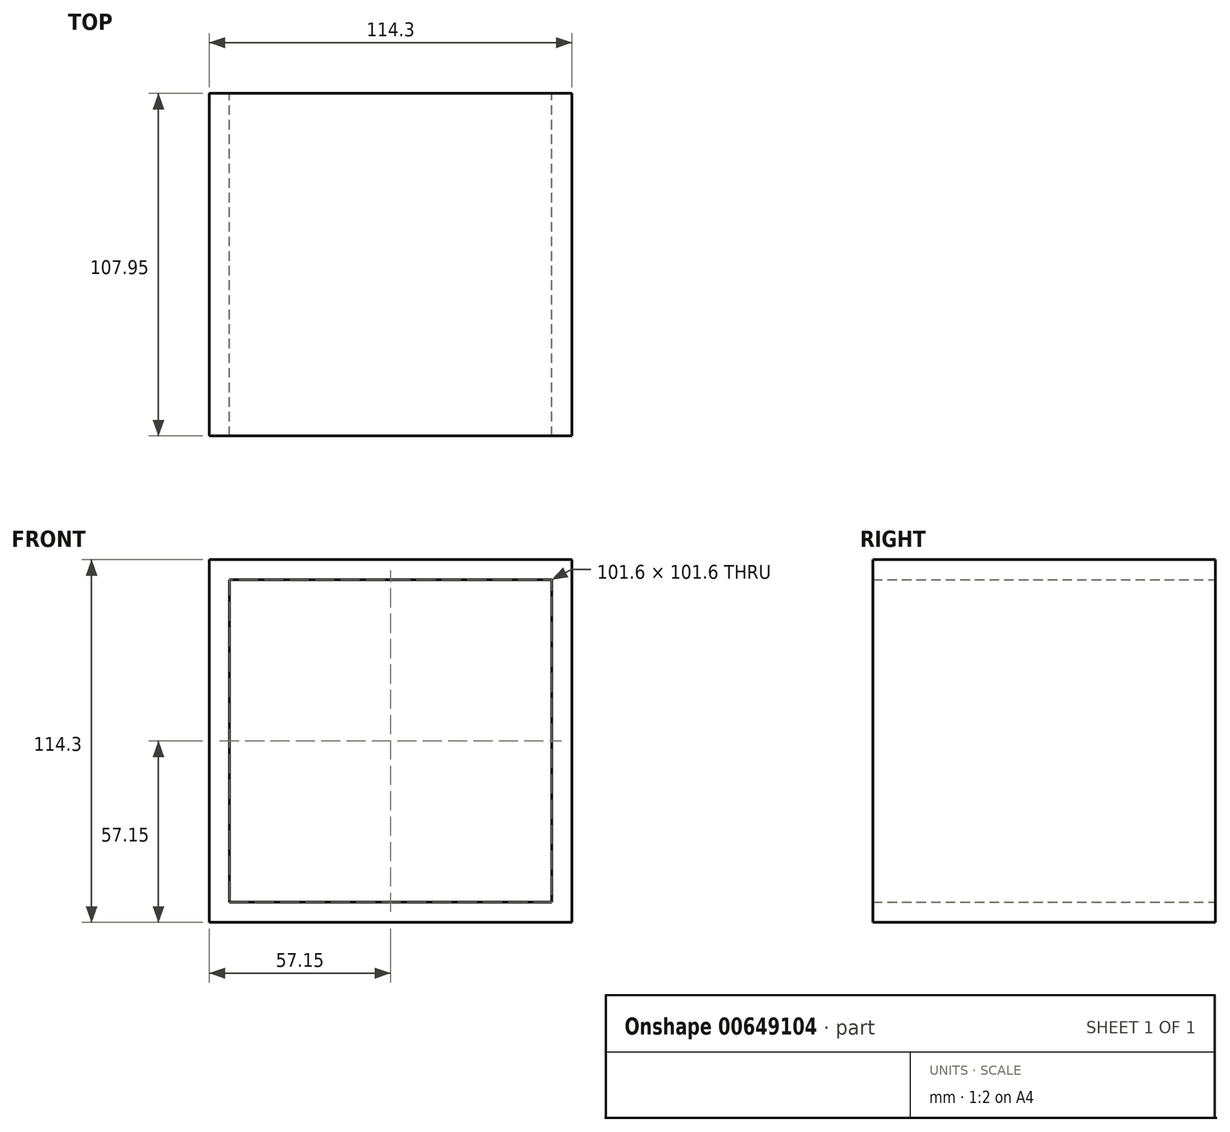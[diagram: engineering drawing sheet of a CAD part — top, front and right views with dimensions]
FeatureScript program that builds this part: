
annotation { "Feature Type Name" : "Feature", "Feature Type Description" : "" }
export const myFeature = defineFeature(function(context is Context, id is Id, definition is map)
    precondition{}
    {
        {
            var Q0;
            Q0=qCreatedBy(makeId("Front.planeOp"),FACE);
            var sketch = newSketch(context, id + "F0", { "sketchPlane" : qUnion([Q0])});
            skLineSegment(sketch, "E0.bottom", {"start": v(50.8, -50.8) * mm, "end": v(-50.8, -50.8) * mm});
            skLineSegment(sketch, "E0.top", {"start": v(50.8, 50.8) * mm, "end": v(-50.8, 50.8) * mm});
            skLineSegment(sketch, "E0.left", {"start": v(50.8, -50.8) * mm, "end": v(50.8, 50.8) * mm});
            skLineSegment(sketch, "E0.right", {"start": v(-50.8, -50.8) * mm, "end": v(-50.8, 50.8) * mm});
            skPoint(sketch, "E0.middle", {"position": v(0, 0) * mm});
            skLineSegment(sketch, "E1.0", {"start": v(57.15, 57.15) * mm, "end": v(-57.15, 57.15) * mm});
            skLineSegment(sketch, "E1.1", {"start": v(57.15, -57.15) * mm, "end": v(57.15, 57.15) * mm});
            skLineSegment(sketch, "E1.2", {"start": v(57.15, -57.15) * mm, "end": v(-57.15, -57.15) * mm});
            skLineSegment(sketch, "E1.3", {"start": v(-57.15, -57.15) * mm, "end": v(-57.15, 57.15) * mm});
            skSolve(sketch);
        }
        {
            var Q0;
            Q0=qSketchRegion(id+"F0",true);
            extrude(context, id + "F1", {"entities" : qUnion([Q0]), "depth" : 107.95 * mm, "offsetDistance" : 25.4 * mm});
        }
    });
